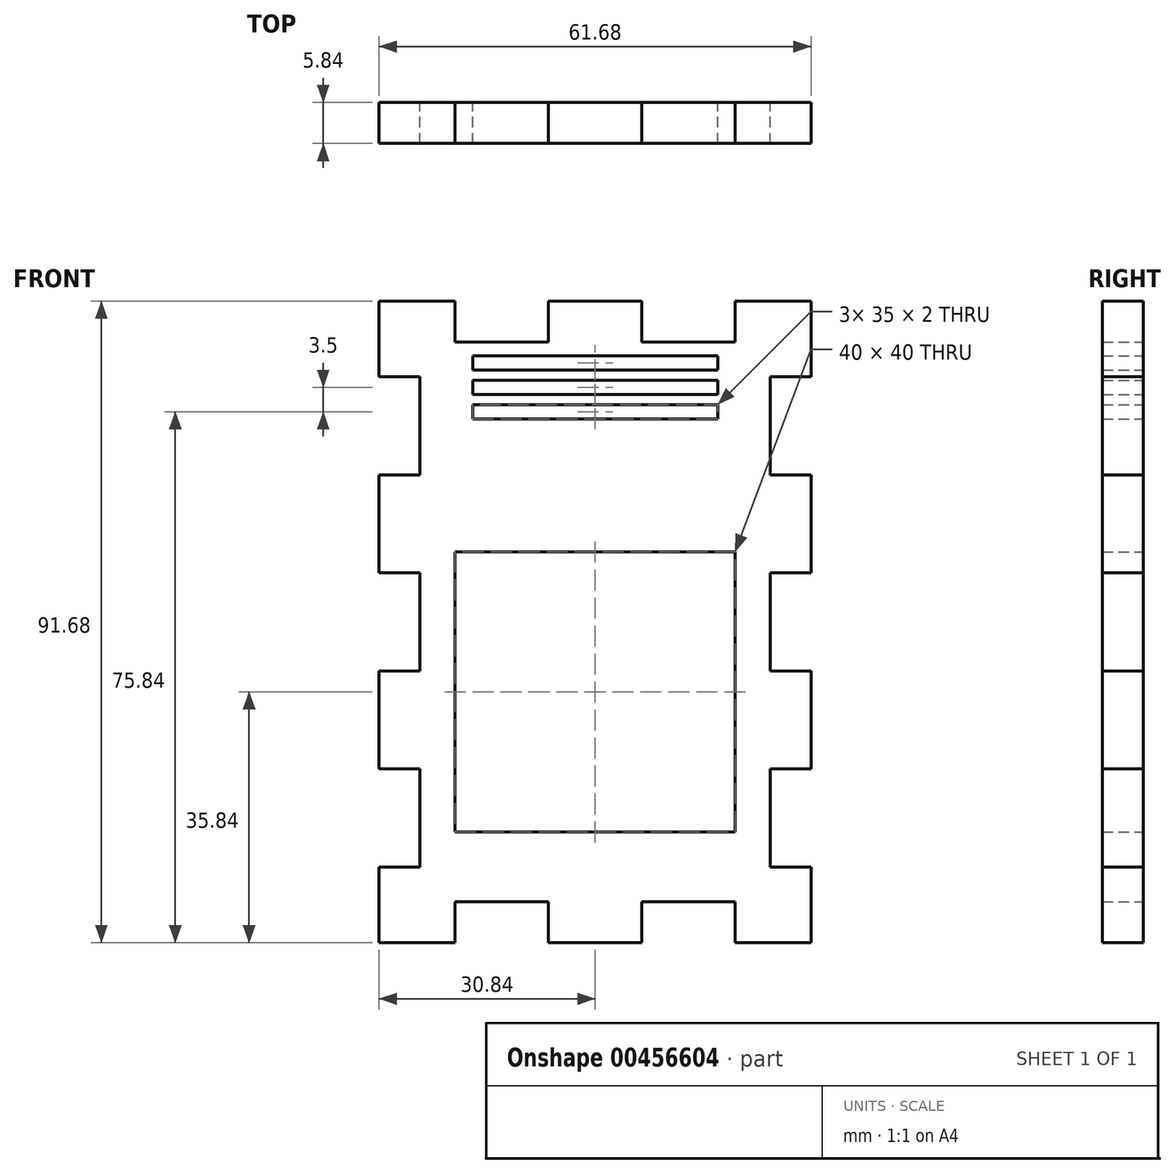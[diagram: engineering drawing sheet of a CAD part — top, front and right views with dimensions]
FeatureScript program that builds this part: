
annotation { "Feature Type Name" : "Feature", "Feature Type Description" : "" }
export const myFeature = defineFeature(function(context is Context, id is Id, definition is map)
    precondition{}
    {
        {
            var Q0;
            Q0=qCreatedBy(makeId("Front.planeOp"),FACE);
            var sketch = newSketch(context, id + "F0", { "sketchPlane" : qUnion([Q0])});
            skLineSegment(sketch, "E0.bottom", {"start": v(-20, -40) * mm, "end": v(-6.67, -40) * mm});
            skLineSegment(sketch, "E0.top", {"start": v(-20, 40) * mm, "end": v(-6.67, 40) * mm});
            skLineSegment(sketch, "E0.left", {"start": v(-25, -35) * mm, "end": v(-25, -21) * mm});
            skLineSegment(sketch, "E0.right", {"start": v(25, -35) * mm, "end": v(25, -21) * mm});
            skLineSegment(sketch, "E1.bottom", {"start": v(-30.84, 45.84) * mm, "end": v(-20, 45.84) * mm});
            skLineSegment(sketch, "E1.top", {"start": v(-30.84, -45.84) * mm, "end": v(-20, -45.84) * mm});
            skLineSegment(sketch, "E1.left", {"start": v(-30.84, 45.84) * mm, "end": v(-30.84, 35) * mm});
            skLineSegment(sketch, "E1.right", {"start": v(30.84, 45.84) * mm, "end": v(30.84, 35) * mm});
            skLineSegment(sketch, "E2.top", {"start": v(-30.84, 35) * mm, "end": v(-25, 35) * mm});
            skLineSegment(sketch, "E2.right", {"start": v(-20, 45.84) * mm, "end": v(-20, 40) * mm});
            skLineSegment(sketch, "E3.bottom", {"start": v(30.84, 45.84) * mm, "end": v(20, 45.84) * mm});
            skLineSegment(sketch, "E3.top", {"start": v(30.84, 35) * mm, "end": v(25, 35) * mm});
            skLineSegment(sketch, "E3.right", {"start": v(20, 45.84) * mm, "end": v(20, 40) * mm});
            skLineSegment(sketch, "E4.top", {"start": v(-6.67, 45.84) * mm, "end": v(6.67, 45.84) * mm});
            skLineSegment(sketch, "E4.left", {"start": v(-6.67, 40) * mm, "end": v(-6.67, 45.84) * mm});
            skLineSegment(sketch, "E4.right", {"start": v(6.67, 40) * mm, "end": v(6.67, 45.84) * mm});
            skLineSegment(sketch, "E5.top", {"start": v(-30.84, -35) * mm, "end": v(-25, -35) * mm});
            skLineSegment(sketch, "E5.left", {"start": v(-30.84, -45.84) * mm, "end": v(-30.84, -35) * mm});
            skLineSegment(sketch, "E5.right", {"start": v(-20, -45.84) * mm, "end": v(-20, -40) * mm});
            skLineSegment(sketch, "E6.bottom", {"start": v(30.84, -45.84) * mm, "end": v(20, -45.84) * mm});
            skLineSegment(sketch, "E6.top", {"start": v(30.84, -35) * mm, "end": v(25, -35) * mm});
            skLineSegment(sketch, "E6.left", {"start": v(30.84, -45.84) * mm, "end": v(30.84, -35) * mm});
            skLineSegment(sketch, "E6.right", {"start": v(20, -45.84) * mm, "end": v(20, -40) * mm});
            skLineSegment(sketch, "E7.bottom", {"start": v(-6.67, -45.84) * mm, "end": v(6.67, -45.84) * mm});
            skLineSegment(sketch, "E7.left", {"start": v(-6.67, -45.84) * mm, "end": v(-6.67, -40) * mm});
            skLineSegment(sketch, "E7.right", {"start": v(6.67, -45.84) * mm, "end": v(6.67, -40) * mm});
            skLineSegment(sketch, "E8.bottom", {"start": v(-30.84, 21) * mm, "end": v(-25, 21) * mm});
            skLineSegment(sketch, "E8.top", {"start": v(-30.84, 7) * mm, "end": v(-25, 7) * mm});
            skLineSegment(sketch, "E8.left", {"start": v(-30.84, 21) * mm, "end": v(-30.84, 7) * mm});
            skLineSegment(sketch, "E9.bottom", {"start": v(-30.84, -7) * mm, "end": v(-25, -7) * mm});
            skLineSegment(sketch, "E9.top", {"start": v(-30.84, -21) * mm, "end": v(-25, -21) * mm});
            skLineSegment(sketch, "E9.left", {"start": v(-30.84, -7) * mm, "end": v(-30.84, -21) * mm});
            skLineSegment(sketch, "E10.bottom", {"start": v(25, 21) * mm, "end": v(30.84, 21) * mm});
            skLineSegment(sketch, "E10.top", {"start": v(25, 7) * mm, "end": v(30.84, 7) * mm});
            skLineSegment(sketch, "E10.right", {"start": v(30.84, 21) * mm, "end": v(30.84, 7) * mm});
            skLineSegment(sketch, "E11.bottom", {"start": v(25, -7) * mm, "end": v(30.84, -7) * mm});
            skLineSegment(sketch, "E11.top", {"start": v(25, -21) * mm, "end": v(30.84, -21) * mm});
            skLineSegment(sketch, "E11.right", {"start": v(30.84, -7) * mm, "end": v(30.84, -21) * mm});
            skLineSegment(sketch, "E12.trimOffspring", {"start": v(20, 45.84) * mm, "end": v(30.84, 45.84) * mm});
            skLineSegment(sketch, "E13.trimOffspring", {"start": v(6.67, 40) * mm, "end": v(20, 40) * mm});
            skLineSegment(sketch, "E14.trimOffspring", {"start": v(-30.84, -35) * mm, "end": v(-30.84, -45.84) * mm});
            skLineSegment(sketch, "E15.trimOffspring", {"start": v(-25, -7) * mm, "end": v(-25, 7) * mm});
            skLineSegment(sketch, "E16.trimOffspring", {"start": v(-25, 21) * mm, "end": v(-25, 35) * mm});
            skLineSegment(sketch, "E17.trimOffspring", {"start": v(25, 21) * mm, "end": v(25, 35) * mm});
            skLineSegment(sketch, "E18.trimOffspring", {"start": v(30.84, -35) * mm, "end": v(30.84, -45.84) * mm});
            skLineSegment(sketch, "E19.trimOffspring", {"start": v(25, -7) * mm, "end": v(25, 7) * mm});
            skLineSegment(sketch, "E20.trimOffspring", {"start": v(20, -45.84) * mm, "end": v(30.84, -45.84) * mm});
            skLineSegment(sketch, "E21.trimOffspring", {"start": v(6.67, -40) * mm, "end": v(20, -40) * mm});
            skLineSegment(sketch, "E22.bottom", {"start": v(20, 10) * mm, "end": v(-20, 10) * mm});
            skLineSegment(sketch, "E22.top", {"start": v(20, -30) * mm, "end": v(-20, -30) * mm});
            skLineSegment(sketch, "E22.left", {"start": v(20, 10) * mm, "end": v(20, -30) * mm});
            skLineSegment(sketch, "E22.right", {"start": v(-20, 10) * mm, "end": v(-20, -30) * mm});
            skLineSegment(sketch, "E23.bottom", {"start": v(17.5, 38) * mm, "end": v(-17.5, 38) * mm});
            skLineSegment(sketch, "E23.top", {"start": v(17.5, 36) * mm, "end": v(-17.5, 36) * mm});
            skLineSegment(sketch, "E23.left", {"start": v(17.5, 38) * mm, "end": v(17.5, 36) * mm});
            skLineSegment(sketch, "E23.right", {"start": v(-17.5, 38) * mm, "end": v(-17.5, 36) * mm});
            skPoint(sketch, "E23.middle", {"position": v(0, 37) * mm});
            skLineSegment(sketch, "E24.bottom", {"start": v(17.5, 34.5) * mm, "end": v(-17.5, 34.5) * mm});
            skLineSegment(sketch, "E24.top", {"start": v(17.5, 32.5) * mm, "end": v(-17.5, 32.5) * mm});
            skLineSegment(sketch, "E24.left", {"start": v(17.5, 34.5) * mm, "end": v(17.5, 32.5) * mm});
            skLineSegment(sketch, "E24.right", {"start": v(-17.5, 34.5) * mm, "end": v(-17.5, 32.5) * mm});
            skPoint(sketch, "E24.middle", {"position": v(0, 33.5) * mm});
            skLineSegment(sketch, "E25.bottom", {"start": v(17.5, 31) * mm, "end": v(-17.5, 31) * mm});
            skLineSegment(sketch, "E25.top", {"start": v(17.5, 29) * mm, "end": v(-17.5, 29) * mm});
            skLineSegment(sketch, "E25.left", {"start": v(17.5, 31) * mm, "end": v(17.5, 29) * mm});
            skLineSegment(sketch, "E25.right", {"start": v(-17.5, 31) * mm, "end": v(-17.5, 29) * mm});
            skPoint(sketch, "E25.middle", {"position": v(0, 30) * mm});
            skSolve(sketch);
        }
        {
            var Q0;
            Q0 = qSketchRegion(id + "F0", true);
            extrude(context, id + "F1", {"entities" : qUnion([Q0]), "depth" : 5.84 * mm});
        }
    });
